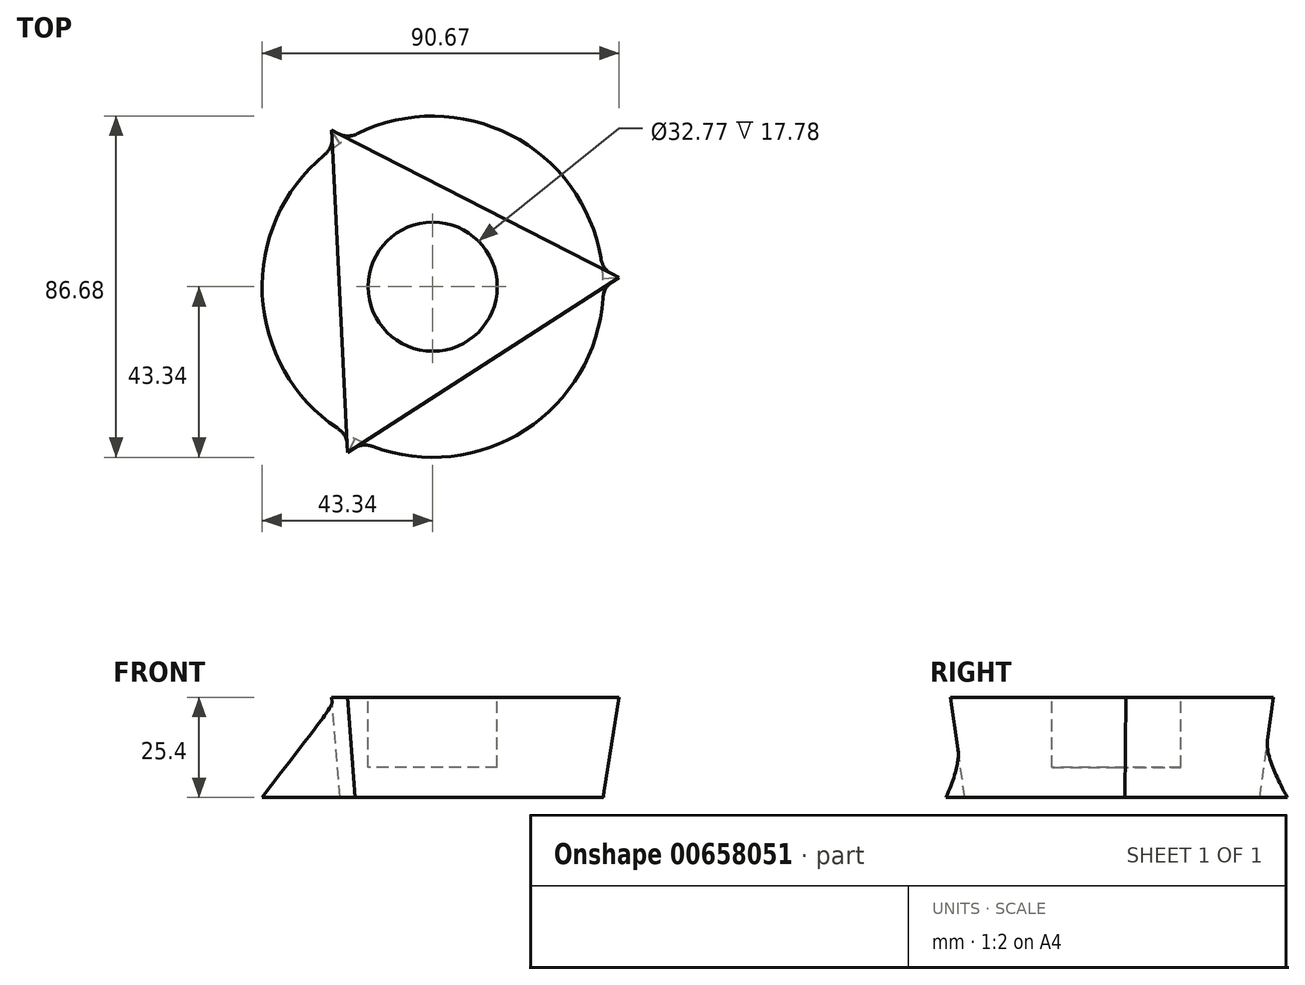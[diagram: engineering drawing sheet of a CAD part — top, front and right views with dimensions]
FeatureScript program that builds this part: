
annotation { "Feature Type Name" : "Feature", "Feature Type Description" : "" }
export const myFeature = defineFeature(function(context is Context, id is Id, definition is map)
    precondition{}
    {
        {
            var Q0;
            Q0=qCreatedBy(makeId("Top.planeOp"),FACE);
            cPlane(context, id + "F0", {"entities" : qUnion([Q0]), "cplaneType" : CPlaneType.OFFSET, "offset" : 25.4 * mm, "width" : 152.4 * mm, "height" : 152.4 * mm});
        }
        {
            var Q0;
            Q0=qCreatedBy(makeId("Top.planeOp"),FACE);
            var sketch = newSketch(context, id + "F1", { "sketchPlane" : qUnion([Q0])});
            skCircle(sketch, "E0", {"center": v(0, 0) * mm, "radius": 43.34 * mm});
            skSolve(sketch);
        }
        {
            var Q0;
            Q0=qCreatedBy(id+"F0.planeOp",FACE);
            var sketch = newSketch(context, id + "F2", { "sketchPlane" : qUnion([Q0])});
            skCircle(sketch, "E1.cCircle", {"center": v(0, 0) * mm, "radius": 23.7 * mm, "construction": true});
            skLineSegment(sketch, "E1.0", {"start": v(-25.7, 39.82) * mm, "end": v(47.33, 2.34) * mm});
            skLineSegment(sketch, "E1.1", {"start": v(47.33, 2.34) * mm, "end": v(-21.64, -42.16) * mm});
            skLineSegment(sketch, "E1.2", {"start": v(-21.64, -42.16) * mm, "end": v(-25.7, 39.82) * mm});
            skPoint(sketch, "E1.0.midPoint", {"position": v(10.82, 21.08) * mm});
            skSolve(sketch);
        }
        {
            var Q0;
            Q0=makeQuery(id+"F1.imprint","IMPRINT",FACE,{"disambiguationData":[TD([[makeQuery(id+"F1.imprint","IMPRINT",EDGE,{"derivedFrom":sQuery(id+"F1.wireOp",EDGE,"E0")}),1.0]])]});
            var Q1;
            Q1=makeQuery(id+"F2.imprint","IMPRINT",FACE,{"disambiguationData":[TD([[makeQuery(id+"F2.imprint","IMPRINT",EDGE,{"derivedFrom":sQuery(id+"F2.wireOp",EDGE,"E1.0")}),-1.0]])]});
            loft(context, id + "F3", {"sheetProfilesArray" : [{ "sheetProfileEntities" : qUnion([Q0]) }, { "sheetProfileEntities" : qUnion([Q1]) }]});
        }
        {
            var Q0;
            Q0=makeQuery(id+"F3.opLoft","CAP_FACE",FACE,{"disambiguationData":[OSD([makeQuery(id+"F2.imprint","IMPRINT",FACE,{"disambiguationData":[TD([[makeQuery(id+"F2.imprint","IMPRINT",EDGE,{"derivedFrom":sQuery(id+"F2.wireOp",EDGE,"E1.0")}),-1.0]])]})])],"isStart":true});
            var sketch = newSketch(context, id + "F4", { "sketchPlane" : qUnion([Q0])});
            skCircle(sketch, "E2", {"center": v(0, 0) * mm, "radius": 16.39 * mm});
            skSolve(sketch);
        }
        {
            var Q0;
            Q0 = qSketchRegion(id + "F4", true);
            extrude(context, id + "F5", {"entities" : qUnion([Q0]), "operationType" : NewBodyOperationType.REMOVE, "oppositeDirection" : true, "depth" : 17.78 * mm, "offsetDistance" : 25.4 * mm});
        }
    });
